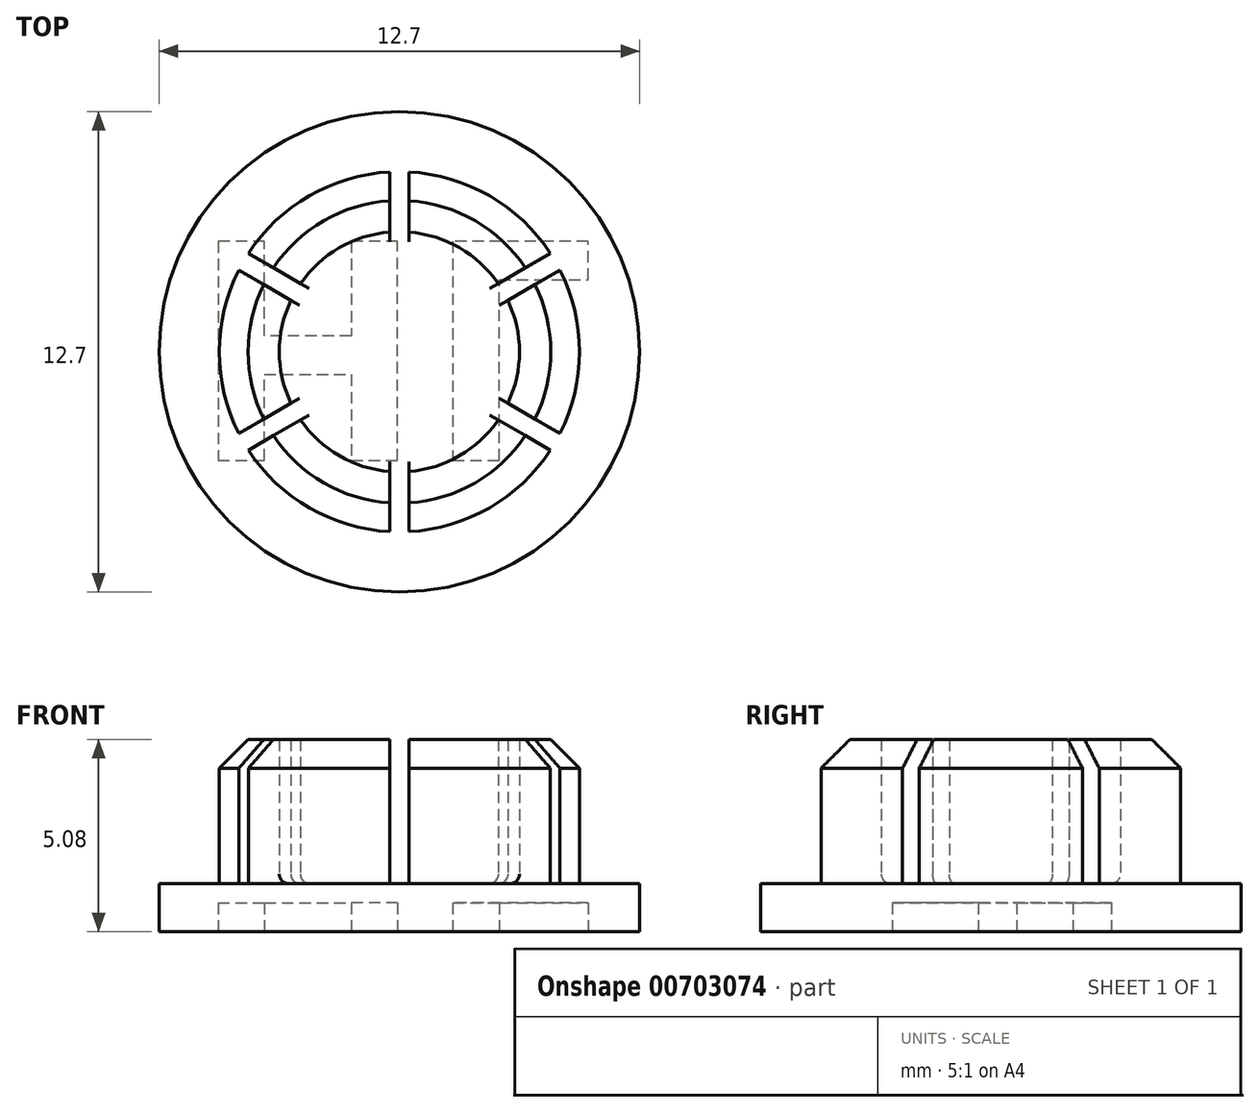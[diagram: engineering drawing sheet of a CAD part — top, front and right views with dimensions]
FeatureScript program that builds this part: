
annotation { "Feature Type Name" : "Feature", "Feature Type Description" : "" }
export const myFeature = defineFeature(function(context is Context, id is Id, definition is map)
    precondition{}
    {
        {
            var Q0;
            Q0=qCreatedBy(makeId("Top.planeOp"),FACE);
            var sketch = newSketch(context, id + "F0", { "sketchPlane" : qUnion([Q0])});
            skCircle(sketch, "E0", {"center": v(0, 0) * mm, "radius": 6.35 * mm});
            skCircle(sketch, "E1", {"center": v(0, 0) * mm, "radius": 4.76 * mm});
            skCircle(sketch, "E2", {"center": v(0, 0) * mm, "radius": 3.18 * mm});
            skSolve(sketch);
        }
        {
            var Q0;
            Q0=makeQuery(id+"F0.imprint","IMPRINT",FACE,{"disambiguationData":[TD([[makeQuery(id+"F0.imprint","IMPRINT",EDGE,{"derivedFrom":sQuery(id+"F0.wireOp",EDGE,"E0")}),1.0]])]});
            var Q1;
            Q1=makeQuery(id+"F0.imprint","IMPRINT",FACE,{"disambiguationData":[TD([[makeQuery(id+"F0.imprint","IMPRINT",EDGE,{"derivedFrom":sQuery(id+"F0.wireOp",EDGE,"E1")}),1.0]])]});
            var Q2;
            Q2=makeQuery(id+"F0.imprint","IMPRINT",FACE,{"disambiguationData":[TD([[makeQuery(id+"F0.imprint","IMPRINT",EDGE,{"derivedFrom":sQuery(id+"F0.wireOp",EDGE,"E2")}),1.0]])]});
            extrude(context, id + "F1", {"entities" : qUnion([Q0, Q1, Q2]), "oppositeDirection" : true, "depth" : 1.27 * mm, "offsetDistance" : 25.4 * mm});
        }
        {
            var Q0;
            Q0=makeQuery(id+"F0.imprint","IMPRINT",FACE,{"disambiguationData":[TD([[makeQuery(id+"F0.imprint","IMPRINT",EDGE,{"derivedFrom":sQuery(id+"F0.wireOp",EDGE,"E1")}),1.0]])]});
            extrude(context, id + "F2", {"entities" : qUnion([Q0]), "operationType" : NewBodyOperationType.ADD, "depth" : 3.8 * mm, "offsetDistance" : 25.4 * mm});
        }
        {
            var Q0;
            Q0=makeQuery(id+"F2.opExtrude","CAP_EDGE",EDGE,{"disambiguationData":[OSD([sQuery(id+"F0.wireOp",EDGE,"E1")])],"isStart":false});
            chamfer(context, id + "F3", {"entities" : qUnion([Q0]), "width" : 0.76 * mm, "tangentPropagation" : true});
        }
        {
            var Q0;
            Q0=makeQuery(id+"F2.opExtrude","CAP_EDGE",EDGE,{"disambiguationData":[OSD([sQuery(id+"F0.wireOp",EDGE,"E2")])],"isStart":true});
            fillet(context, id + "F4", {"entities" : qUnion([Q0]), "radius" : 0.25 * mm, "tangentPropagation" : true, "allowEdgeOverflow" : false});
        }
        {
            var Q0;
            Q0=makeQuery(id+"F2.opExtrude","CAP_FACE",FACE,{"disambiguationData":[OSD([sQuery(id+"F0.wireOp",EDGE,"E1"),sQuery(id+"F0.wireOp",EDGE,"E2")])],"isStart":false});
            var sketch = newSketch(context, id + "F5", { "sketchPlane" : qUnion([Q0])});
            skLineSegment(sketch, "E3.bottom", {"start": v(0.25, 5.02) * mm, "end": v(-0.25, 5.02) * mm});
            skLineSegment(sketch, "E3.top", {"start": v(0.25, -5.02) * mm, "end": v(-0.25, -5.02) * mm});
            skLineSegment(sketch, "E3.left", {"start": v(0.25, 5.02) * mm, "end": v(0.25, -5.02) * mm});
            skLineSegment(sketch, "E3.right", {"start": v(-0.25, 5.02) * mm, "end": v(-0.25, -5.02) * mm});
            skPoint(sketch, "E3.middle", {"position": v(0, 0) * mm});
            skSolve(sketch);
        }
        {
            var Q0;
            {var subQ0=sQuery(id+"F5.wireOp",EDGE,"E3.top");Q0=makeQuery(id+"F5.imprint","IMPRINT",FACE,{"disambiguationData":[TD([[makeQuery(id+"F5.imprint","IMPRINT",EDGE,{"derivedFrom":subQ0}),-1.0]])]});}
            var Q1;
            {var subQ0=sQuery(id+"F5.wireOp",EDGE,"E3.left");var subQ1=sQuery(id+"F0.wireOp",EDGE,"E2");var subQ5=makeQuery(id+"F2.opExtrude","CAP_EDGE",EDGE,{"disambiguationData":[OSD([subQ1])],"isStart":false});var subQ6=makeQuery(id+"F5.imprint","INTERSECT",VERTEX,{"disambiguationData":[OD(1.0)],"derivedFrom":[subQ5,subQ0]});Q1=makeQuery(id+"F5.imprint","IMPRINT",FACE,{"disambiguationData":[TD([[makeQuery(id+"F5.imprint","IMPRINT",EDGE,{"disambiguationData":[TD([[subQ6,1.0]])],"derivedFrom":subQ5}),-1.0]])]});}
            var Q2;
            {var subQ0=sQuery(id+"F5.wireOp",EDGE,"E3.left");var subQ1=makeQuery(id+"F2.opExtrude","CAP_EDGE",EDGE,{"disambiguationData":[OSD([sQuery(id+"F0.wireOp",EDGE,"E2")])],"isStart":false});var subQ2=makeQuery(id+"F5.imprint","INTERSECT",VERTEX,{"disambiguationData":[OD(0.0)],"derivedFrom":[subQ1,subQ0]});Q2=makeQuery(id+"F5.imprint","IMPRINT",FACE,{"disambiguationData":[TD([[makeQuery(id+"F5.imprint","IMPRINT",EDGE,{"disambiguationData":[TD([[subQ2,-1.0]])],"derivedFrom":subQ0}),-1.0]])]});}
            var Q3;
            {var subQ0=sQuery(id+"F5.wireOp",EDGE,"E3.left");var subQ1=sQuery(id+"F0.wireOp",EDGE,"E2");var subQ5=makeQuery(id+"F2.opExtrude","CAP_EDGE",EDGE,{"disambiguationData":[OSD([subQ1])],"isStart":false});var subQ6=makeQuery(id+"F5.imprint","INTERSECT",VERTEX,{"disambiguationData":[OD(0.0)],"derivedFrom":[subQ5,subQ0]});Q3=makeQuery(id+"F5.imprint","IMPRINT",FACE,{"disambiguationData":[TD([[makeQuery(id+"F5.imprint","IMPRINT",EDGE,{"disambiguationData":[TD([[subQ6,-1.0]])],"derivedFrom":subQ5}),-1.0]])]});}
            var Q4;
            {var subQ0=sQuery(id+"F5.wireOp",EDGE,"E3.bottom");Q4=makeQuery(id+"F5.imprint","IMPRINT",FACE,{"disambiguationData":[TD([[makeQuery(id+"F5.imprint","IMPRINT",EDGE,{"derivedFrom":subQ0}),1.0]])]});}
            extrude(context, id + "F6", {"entities" : qUnion([Q0, Q1, Q2, Q3, Q4]), "oppositeDirection" : true, "depth" : 3.8 * mm, "offsetDistance" : 25.4 * mm});
        }
        {
            var Q0;
            Q0=qCreatedBy(makeId("Front.planeOp"),FACE);
            var sketch = newSketch(context, id + "F7", { "sketchPlane" : qUnion([Q0])});
            skLineSegment(sketch, "E4", {"start": v(0, 0) * mm, "end": v(0, 21.33) * mm, "construction": true});
            skSolve(sketch);
        }
        {
            var Q0;
            Q0=makeQuery(id+"F6.opExtrude","SWEPT_BODY",BODY,{"disambiguationData":[OSD([sQuery(id+"F5.wireOp",EDGE,"E3.bottom"),sQuery(id+"F5.wireOp",EDGE,"E3.top"),sQuery(id+"F5.wireOp",EDGE,"E3.left"),sQuery(id+"F5.wireOp",EDGE,"E3.right")])]});
            var Q1;
            Q1=sQuery(id+"F7.wireOp",EDGE,"E4");
            circularPattern(context, id + "F8", {"operationType" : NewBodyOperationType.REMOVE, "entities" : qUnion([Q0]), "axis" : qUnion([Q1]), "angle" : 360 * degree, "instanceCount" : 3, "equalSpace" : true});
        }
        {
            var Q0;
            Q0=makeQuery(id+"F1.opExtrude","CAP_FACE",FACE,{"disambiguationData":[OSD([sQuery(id+"F0.wireOp",EDGE,"E0")])],"isStart":false});
            var sketch = newSketch(context, id + "F9", { "sketchPlane" : qUnion([Q0])});
            skText(sketch, "E5", { "text": "HL", "fontName": "OpenSans-Bold.ttf"});
            const initialGuessF9  = {"E5": [-0.00552, -0.00292, 1, 0, 0.00584]};
            skSetInitialGuess(sketch, initialGuessF9);
            skSolve(sketch);
        }
        {
            var Q0;
            Q0=makeQuery(id+"F9.imprint","IMPRINT",FACE,{"disambiguationData":[TD([[makeQuery(id+"F9.imprint","IMPRINT",EDGE,{"derivedFrom":sQuery(id+"F9.wireOp",EDGE,"E5.sketch_text.stroke-0")}),-1.0]])]});
            var Q1;
            Q1=makeQuery(id+"F9.imprint","IMPRINT",FACE,{"disambiguationData":[TD([[makeQuery(id+"F9.imprint","IMPRINT",EDGE,{"derivedFrom":sQuery(id+"F9.wireOp",EDGE,"E5.sketch_text.stroke-12")}),-1.0]])]});
            extrude(context, id + "F10", {"entities" : qUnion([Q0, Q1]), "operationType" : NewBodyOperationType.REMOVE, "oppositeDirection" : true, "depth" : 0.76 * mm, "offsetDistance" : 25.4 * mm});
        }
    });
